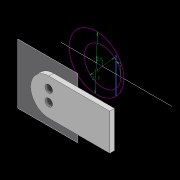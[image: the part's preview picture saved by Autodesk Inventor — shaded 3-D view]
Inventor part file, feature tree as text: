
AUTODESK INVENTOR PART (.ipt)
format: ipt  version: 2022.2 (Build 262287010, 287A)  size: 109,568 bytes
history: native  units: mm
features: sketch x3, extrude x3, hole x1, draft x1, plane x1
ambient origin geometry x8: Origin, YZ Plane, XZ Plane, XY Plane, X Axis, Y Axis, Z Axis, Center Point
bodies: Solid1 (feature_tree)
feature tree (9):
  sketch  "Sketch1"  dims[d0=22.5mm d1=2.5mm]
  extrude  "Extrusion1"  Depth=2.5mm
  extrude  "Extrusion2"  Depth=2.0mm
  hole  "Hole1"  [1 undecoded]
  draft  "FaceDraft1"
  plane  "Work Plane1"
  extrude  "Extrusion3"  Depth=2.0mm
  sketch  "Sketch2"  dims[d2=15.0mm d3=2.0mm]
  sketch  "Sketch3"  dims[d4=2.5mm d5=0.0mm d6=11.0mm d7=0.0mm d8=3.0mm d10=3.0mm d11=6.0mm d12=4.0mm d13=2.0mm d14=90.0deg d15=4.0mm d16=0.0mm d17=20.0mm d18=25.0mm d19=25.0mm d20=2.0mm d21=0.0mm d22=0.436332mm d23=5.5mm]
note: 1 required parameter value undecoded (feature->parameter linkage not recoverable at this tier; creation-order binding heuristic only, values carry confidence <= 0.55)
